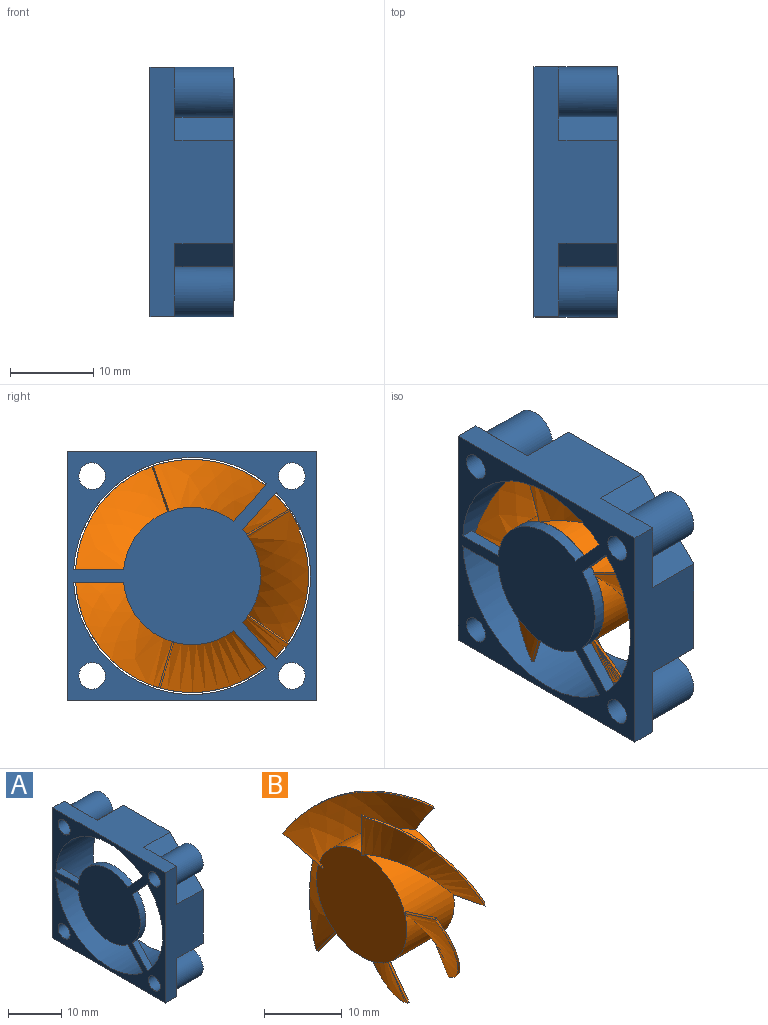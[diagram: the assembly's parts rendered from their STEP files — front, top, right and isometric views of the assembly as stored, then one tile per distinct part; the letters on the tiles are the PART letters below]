
ASSEMBLY  parts=2 mates=1
PART A: 45 faces, bbox 10x30x30 mm
  f0: plane 30x10mm, normal (0,1,0), area 177mm2, adj f2,f6,f10,f18,f19,f24,f25,f40
  f1: cylinder r=1.6mm len=10mm, axis (1,0,0), area 100.5mm2, adj f6,f24
  f2: plane 30x10mm, normal (0,0,-1), area 177mm2, adj f0,f6,f8,f9,f11,f15,f16,f24
  f3: plane 5.79x2.79mm, normal (1,0,0), area 5.8mm2, adj f9,f12,f23
  f4: plane 3x3mm, normal (1,0,0), area 1.9mm2, adj f9,f23,f25
  f5: plane 5.79x2.79mm, normal (1,0,0), area 5.8mm2, adj f9,f13,f14
  f6: plane 30x30mm, normal (-1,0,0), area 470.7mm2, adj f0,f1,f2,f7,f9,f25,f26,f27
  f7: cylinder r=1.6mm len=10mm, axis (1,0,0), area 100.5mm2, adj f6,f24
  f8: plane 3x3mm, normal (1,0,0), area 1.9mm2, adj f2,f9,f14
  f9: plane 30x10mm, normal (0,-1,0), area 177mm2, adj f2,f3,f4,f5,f6,f8,f12,f13
  f10: plane 5.79x2.79mm, normal (1,0,0), area 5.8mm2, adj f0,f19,f20
  f11: plane 5.79x2.79mm, normal (1,0,0), area 5.8mm2, adj f2,f14,f15
  f12: plane 7x2.79mm, normal (0,-0.71,0.71), area 27.7mm2, adj f3,f9,f23,f24
  f13: plane 7x2.79mm, normal (0,-0.71,-0.71), area 27.7mm2, adj f5,f9,f14,f24
  f14: cylinder r=3mm len=7mm, axis (1,0,0), area 96.1mm2, adj f5,f8,f11,f13,f15,f24
  f15: plane 7x2.79mm, normal (0,-0.71,-0.71), area 27.7mm2, adj f2,f11,f14,f24
  f16: plane 7x2.79mm, normal (0,0.71,-0.71), area 27.7mm2, adj f2,f17,f24,f44
  f17: cylinder r=3mm len=7mm, axis (1,0,0), area 96.1mm2, adj f16,f18,f24,f42,f43,f44
  f18: plane 7x2.79mm, normal (0,0.71,-0.71), area 27.7mm2, adj f0,f17,f24,f42
  f19: plane 7x2.79mm, normal (0,0.71,0.71), area 27.7mm2, adj f0,f10,f20,f24
  f20: cylinder r=3mm len=7mm, axis (1,0,0), area 96.1mm2, adj f10,f19,f21,f24,f39,f40
  f21: plane 7x2.79mm, normal (0,0.71,0.71), area 27.7mm2, adj f20,f24,f25,f39
  f22: plane 7x2.79mm, normal (0,-0.71,0.71), area 27.7mm2, adj f23,f24,f25,f41
  f23: cylinder r=3mm len=7mm, axis (1,0,0), area 96.1mm2, adj f3,f4,f12,f22,f24,f41
  f24: plane 30x30mm, normal (1,0,0), area 175.7mm2, adj f0,f1,f2,f7,f9,f12,f13,f14
  f25: plane 30x10mm, normal (0,0,1), area 177mm2, adj f0,f4,f6,f9,f21,f22,f24,f39
  f26: cylinder r=14.25mm len=28.5mm, axis (1,0,0), area 888.6mm2, adj f6,f24,f29,f30,f33,f35,f36,f37
  f27: cylinder r=1.6mm len=10mm, axis (1,0,0), area 100.5mm2, adj f6,f24
  f28: cylinder r=1.6mm len=10mm, axis (1,0,0), area 100.5mm2, adj f6,f24
  f29: plane 6.01x1.5mm, normal (0,0,1), area 9mm2, adj f6,f26,f31,f38
  f30: plane 6.01x1.5mm, normal (0,0,-1), area 9mm2, adj f6,f26,f34,f38
  f31: cylinder r=8.25mm len=13.17mm, axis (1,0,0), area 26.3mm2, adj f6,f29,f37,f38
  f32: cylinder r=8.25mm len=11.18mm, axis (1,0,0), area 18.4mm2, adj f6,f33,f36,f38
  f33: plane 4.46x4.03mm, normal (0,-0.74,-0.67), area 9mm2, adj f6,f26,f32,f38
  f34: cylinder r=8.25mm len=13.17mm, axis (1,0,0), area 26.3mm2, adj f6,f30,f35,f38
  f35: plane 4.46x4.03mm, normal (0,0.74,-0.67), area 9mm2, adj f6,f26,f34,f38
  f36: plane 4.46x4.03mm, normal (0,-0.74,0.67), area 9mm2, adj f6,f26,f32,f38
  f37: plane 4.46x4.03mm, normal (0,0.74,0.67), area 9mm2, adj f6,f26,f31,f38
  f38: plane 24.35x22.11mm, normal (1,0,0), area 240.8mm2, adj f26,f29,f30,f31,f32,f33,f34,f35
  f39: plane 5.79x2.79mm, normal (1,0,0), area 5.8mm2, adj f20,f21,f25
  f40: plane 3x3mm, normal (1,0,0), area 1.9mm2, adj f0,f20,f25
  f41: plane 5.79x2.79mm, normal (1,0,0), area 5.8mm2, adj f22,f23,f25
  f42: plane 5.79x2.79mm, normal (1,0,0), area 5.8mm2, adj f0,f17,f18
  f43: plane 3x3mm, normal (1,0,0), area 1.9mm2, adj f0,f2,f17
  f44: plane 5.79x2.79mm, normal (1,0,0), area 5.8mm2, adj f2,f16,f17
PART B: 33 faces, bbox 10.9x28.7x28.8 mm
  f0: plane 26.97x25.52mm, normal (1,0,0), area 228.4mm2, adj f1,f6,f8,f9,f10,f11,f12,f14
  f1: bspline ~16.32x9.32mm, area 97.6mm2, adj f0,f2,f10,f29
  f2: plane 4.8x3.56mm, normal (-0.61,-0.64,-0.46), area 1.7mm2, adj f1,f10,f20,f29
  f3: bspline ~2.5x1.41mm, area 0.8mm2, adj f4,f9,f18,f19
  f4: plane 0.7x0.42mm, normal (1,0,0), area 0.1mm2, adj f3,f9,f19,f30
  f5: plane 6.19x0.24mm, normal (-0.61,0.79,0), area 1.8mm2, adj f7,f15,f16,f27,f32
  f6: cylinder r=14mm len=13.79mm, axis (-1,0,0), area 6.1mm2, adj f0,f15,f27,f32
  f7: cylinder r=14.82mm len=0.75mm, axis (0.99,0.15,0), area 0.1mm2, adj f5,f15,f27
  f8: cylinder r=8.2mm len=14.98mm, axis (1,0,0), area 80.2mm2, adj f0,f13,f24,f26,f27
  f9: bspline ~17.8x11.77mm, area 111.1mm2, adj f0,f3,f4,f12,f13,f17,f18,f30
  f10: cylinder r=8.2mm len=13.02mm, axis (1,0,0), area 84.4mm2, adj f0,f1,f2,f13,f22
  f11: cylinder r=8.2mm len=13.24mm, axis (1,0,0), area 84.4mm2, adj f0,f13,f21,f23,f25
  f12: cylinder r=8.2mm len=15.63mm, axis (1,0,0), area 84.3mm2, adj f0,f9,f13,f32
  f13: plane 16.4x16.4mm, normal (-1,0,0), area 211mm2, adj f8,f9,f10,f11,f12,f14,f16,f17
  f14: cylinder r=8.2mm len=14.83mm, axis (1,0,0), area 88.5mm2, adj f0,f13,f19,f20
  f15: plane 0.72x0.22mm, normal (1,0,0), area 0.1mm2, adj f5,f6,f7,f27
  f16: bspline ~0.49x0.47mm, area 0.1mm2, adj f5,f13,f27
  f17: bspline ~0.88x0.32mm, area 0.1mm2, adj f9,f13,f18
  f18: plane 6.21x2.88mm, normal (-0.61,0.24,-0.75), area 1.9mm2, adj f3,f9,f17,f19
  f19: bspline ~17.18x11.56mm, area 108.1mm2, adj f0,f3,f4,f14,f18,f30
  f20: bspline ~16.87x9.18mm, area 100.4mm2, adj f0,f2,f14,f29
  f21: bspline ~18.71x9.2mm, area 97.6mm2, adj f0,f11,f25,f28
  f22: bspline ~17.47x8.59mm, area 100.4mm2, adj f0,f10,f25,f28
  f23: bspline ~17.47x11.48mm, area 100.4mm2, adj f0,f11,f26,f31
  f24: bspline ~17.33x11.26mm, area 97.6mm2, adj f0,f8,f26,f31
  f25: plane 4.8x3.56mm, normal (-0.61,-0.64,0.46), area 1.7mm2, adj f11,f21,f22,f28
  f26: plane 5.58x1.97mm, normal (-0.61,0.24,0.75), area 1.7mm2, adj f8,f23,f24,f31
  f27: bspline ~13.81x12.91mm, area 103.3mm2, adj f0,f5,f6,f7,f8,f13,f15,f16
  f28: cylinder r=14mm len=17.62mm, axis (-1,0,0), area 6mm2, adj f0,f21,f22,f25
  f29: cylinder r=14mm len=16.97mm, axis (-1,0,0), area 6mm2, adj f0,f1,f2,f20
  f30: cylinder r=14mm len=16.86mm, axis (-1,0,0), area 6mm2, adj f0,f4,f9,f19
  f31: cylinder r=14mm len=16.54mm, axis (-1,0,0), area 6mm2, adj f0,f23,f24,f26
  f32: bspline ~14.15x13.49mm, area 100.4mm2, adj f0,f5,f6,f12
PLACE A t=(8.44,32.71,-9.43)mm fixed
PLACE B rot(axis=(1,0,0),124.6deg) t=(8.44,32.71,-9.43)mm
MATE revolute B.f6 <-> A.f26  axis (-1,0,0) through (9.94,32.71,-9.43)mm
